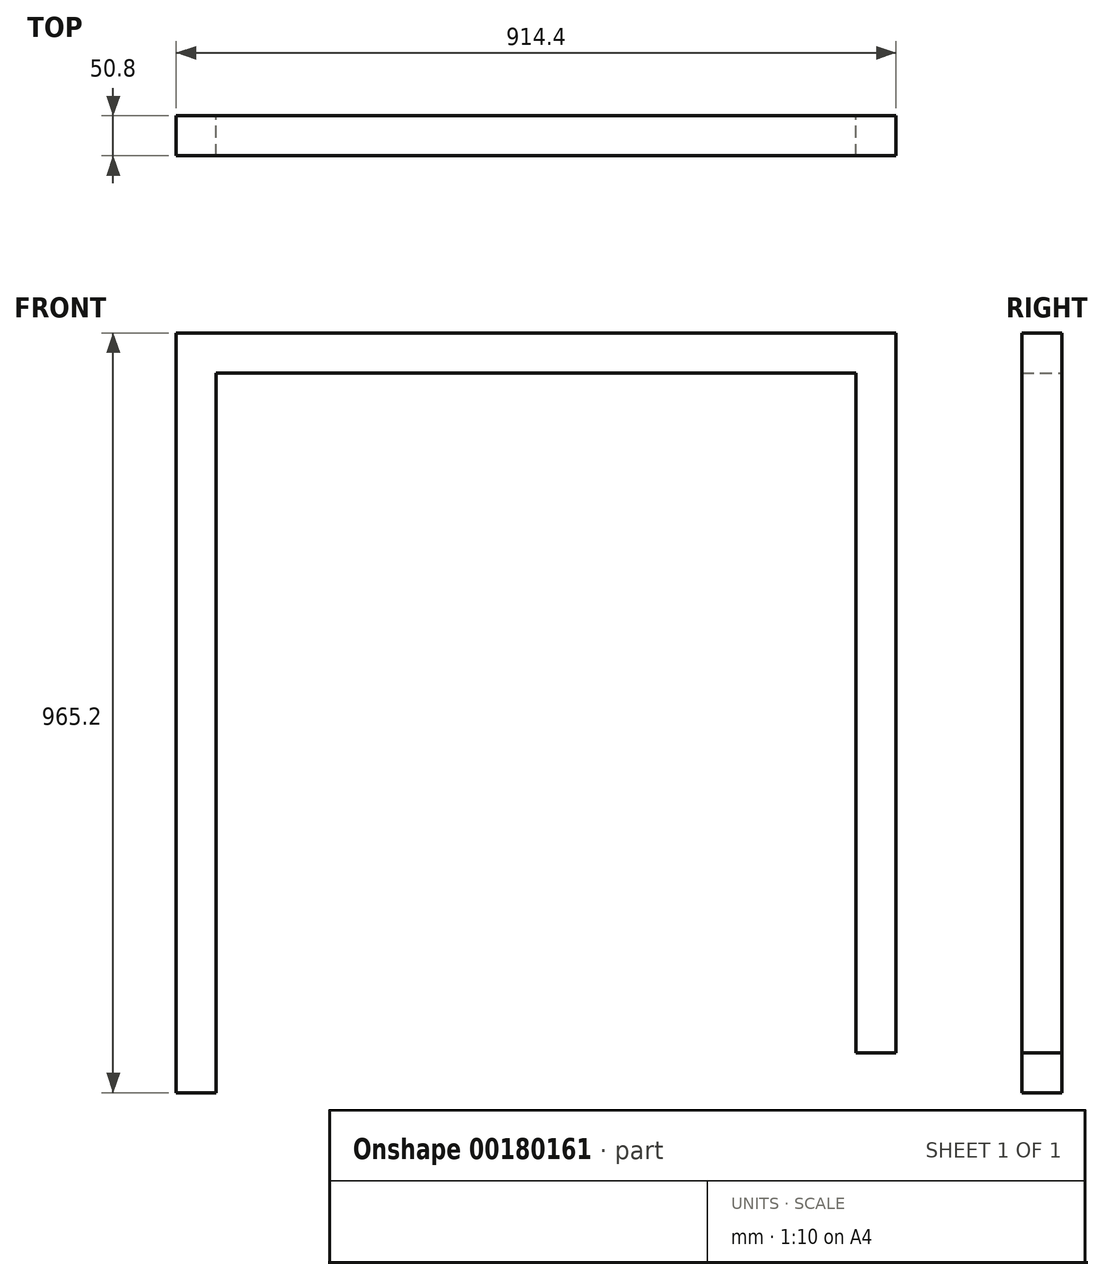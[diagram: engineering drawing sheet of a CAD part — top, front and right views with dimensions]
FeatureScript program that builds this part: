
annotation { "Feature Type Name" : "Feature", "Feature Type Description" : "" }
export const myFeature = defineFeature(function(context is Context, id is Id, definition is map)
    precondition{}
    {
        {
            var Q0;
            Q0=qCreatedBy(makeId("Front.planeOp"),FACE);
            var sketch = newSketch(context, id + "F0", { "sketchPlane" : qUnion([Q0])});
            skLineSegment(sketch, "E0.bottom", {"start": v(0, 0) * mm, "end": v(-50.8, 0) * mm});
            skLineSegment(sketch, "E0.top", {"start": v(0, 914.4) * mm, "end": v(-50.8, 914.4) * mm});
            skLineSegment(sketch, "E0.left", {"start": v(0, 0) * mm, "end": v(0, 914.4) * mm});
            skLineSegment(sketch, "E0.right", {"start": v(-50.8, 0) * mm, "end": v(-50.8, 863.6) * mm});
            skLineSegment(sketch, "E1.bottom", {"start": v(-50.8, 914.4) * mm, "end": v(-914.4, 914.4) * mm});
            skLineSegment(sketch, "E1.top", {"start": v(-50.8, 863.6) * mm, "end": v(-863.6, 863.6) * mm});
            skLineSegment(sketch, "E1.right", {"start": v(-914.4, 914.4) * mm, "end": v(-914.4, 863.6) * mm});
            skLineSegment(sketch, "E2.top", {"start": v(-914.4, -50.8) * mm, "end": v(-863.6, -50.8) * mm});
            skLineSegment(sketch, "E2.left", {"start": v(-914.4, 863.6) * mm, "end": v(-914.4, -50.8) * mm});
            skLineSegment(sketch, "E2.right", {"start": v(-863.6, 863.6) * mm, "end": v(-863.6, -50.8) * mm});
            skSolve(sketch);
        }
        {
            var Q0;
            Q0=makeQuery(id+"F0.imprint","IMPRINT",FACE,{"disambiguationData":[TD([[makeQuery(id+"F0.imprint","IMPRINT",EDGE,{"derivedFrom":sQuery(id+"F0.wireOp",EDGE,"E0.bottom")}),-1.0]])]});
            extrude(context, id + "F1", {"entities" : qUnion([Q0]), "depth" : 50.8 * mm});
        }
    });
